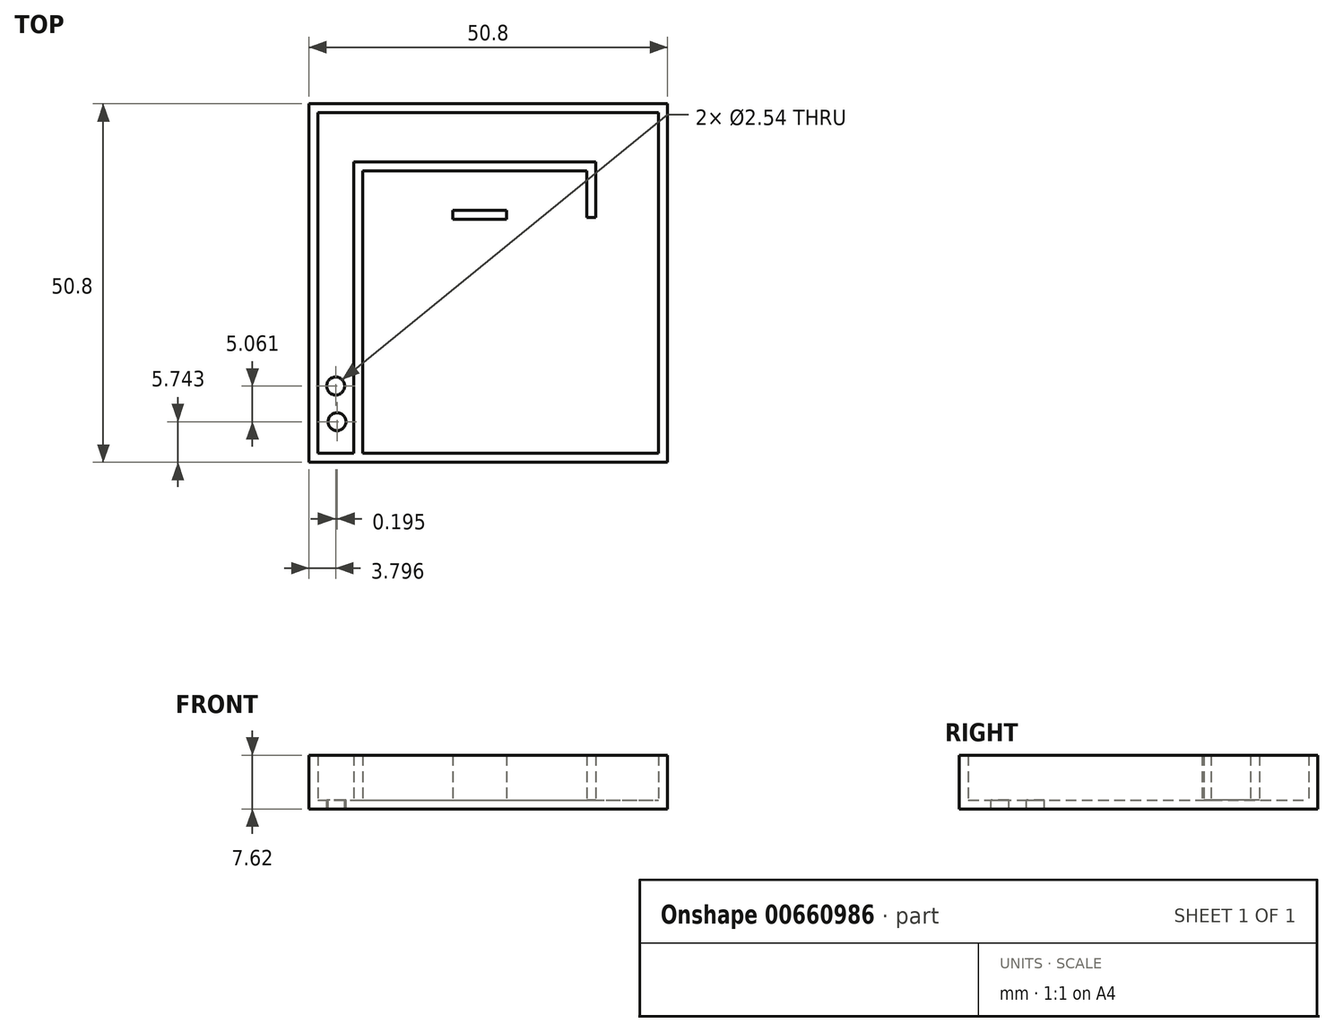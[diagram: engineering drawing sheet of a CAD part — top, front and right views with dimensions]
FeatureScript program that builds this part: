
annotation { "Feature Type Name" : "Feature", "Feature Type Description" : "" }
export const myFeature = defineFeature(function(context is Context, id is Id, definition is map)
    precondition{}
    {
        {
            var Q0;
            Q0=qCreatedBy(makeId("Top.planeOp"),FACE);
            var sketch = newSketch(context, id + "F0", { "sketchPlane" : qUnion([Q0])});
            skLineSegment(sketch, "E0.bottom", {"start": v(0, 0) * mm, "end": v(50.8, 0) * mm});
            skLineSegment(sketch, "E0.top", {"start": v(0, 50.8) * mm, "end": v(50.8, 50.8) * mm});
            skLineSegment(sketch, "E0.left", {"start": v(0, 0) * mm, "end": v(0, 50.8) * mm});
            skLineSegment(sketch, "E0.right", {"start": v(50.8, 0) * mm, "end": v(50.8, 50.8) * mm});
            skSolve(sketch);
        }
        {
            var Q0;
            Q0 = qSketchRegion(id + "F0", true);
            extrude(context, id + "F1", {"entities" : qUnion([Q0]), "depth" : 7.62 * mm, "offsetDistance" : 25.4 * mm});
        }
        {
            var Q0;
            Q0=makeQuery(id+"F1.opExtrude","CAP_FACE",FACE,{"disambiguationData":[OSD([sQuery(id+"F0.wireOp",EDGE,"E0.bottom"),sQuery(id+"F0.wireOp",EDGE,"E0.top"),sQuery(id+"F0.wireOp",EDGE,"E0.left"),sQuery(id+"F0.wireOp",EDGE,"E0.right")])],"isStart":false});
            shell(context, id + "F2", {"entities" : qUnion([Q0]), "thickness" : 1.27 * mm});
        }
        {
            var Q0;
            Q0=makeQuery(id+"F2.opShell","OFFSET_FACE",FACE,{"disambiguationData":[OSD([sQuery(id+"F0.wireOp",EDGE,"E0.bottom"),sQuery(id+"F0.wireOp",EDGE,"E0.top"),sQuery(id+"F0.wireOp",EDGE,"E0.left"),sQuery(id+"F0.wireOp",EDGE,"E0.right")])]});
            var sketch = newSketch(context, id + "F3", { "sketchPlane" : qUnion([Q0])});
            skLineSegment(sketch, "E1", {"start": v(1.27, 1.27) * mm, "end": v(6.35, 1.27) * mm});
            skLineSegment(sketch, "E2.bottom", {"start": v(6.35, 1.27) * mm, "end": v(7.62, 1.27) * mm});
            skLineSegment(sketch, "E2.top", {"start": v(6.35, 42.55) * mm, "end": v(7.62, 42.55) * mm});
            skLineSegment(sketch, "E2.left", {"start": v(6.35, 1.27) * mm, "end": v(6.35, 42.55) * mm});
            skLineSegment(sketch, "E2.right", {"start": v(7.62, 1.27) * mm, "end": v(7.62, 42.55) * mm});
            skLineSegment(sketch, "E3.bottom", {"start": v(7.62, 42.55) * mm, "end": v(40.64, 42.55) * mm});
            skLineSegment(sketch, "E3.top", {"start": v(7.62, 41.28) * mm, "end": v(40.64, 41.28) * mm});
            skLineSegment(sketch, "E3.left", {"start": v(7.62, 42.55) * mm, "end": v(7.62, 41.28) * mm});
            skLineSegment(sketch, "E3.right", {"start": v(40.64, 42.55) * mm, "end": v(40.64, 41.28) * mm});
            skLineSegment(sketch, "E4.bottom", {"start": v(40.64, 41.28) * mm, "end": v(39.37, 41.28) * mm});
            skLineSegment(sketch, "E4.top", {"start": v(40.64, 34.67) * mm, "end": v(39.37, 34.67) * mm});
            skLineSegment(sketch, "E4.left", {"start": v(40.64, 41.28) * mm, "end": v(40.64, 34.67) * mm});
            skLineSegment(sketch, "E4.right", {"start": v(39.37, 41.28) * mm, "end": v(39.37, 34.67) * mm});
            skLineSegment(sketch, "E5.bottom", {"start": v(20.37, 34.42) * mm, "end": v(28, 34.42) * mm});
            skLineSegment(sketch, "E5.top", {"start": v(20.37, 35.69) * mm, "end": v(28, 35.69) * mm});
            skLineSegment(sketch, "E5.left", {"start": v(20.37, 34.42) * mm, "end": v(20.37, 35.69) * mm});
            skLineSegment(sketch, "E5.right", {"start": v(28, 34.42) * mm, "end": v(28, 35.69) * mm});
            skPoint(sketch, "E6.oppositeSnap0", {"position": v(49.53, 25.4) * mm});
            skSolve(sketch);
        }
        {
            var Q0;
            Q0 = qSketchRegion(id + "F3", true);
            extrude(context, id + "F4", {"entities" : qUnion([Q0]), "operationType" : NewBodyOperationType.ADD, "depth" : 6.35 * mm, "offsetDistance" : 25.4 * mm});
        }
        {
            var Q0;
            Q0=makeQuery(id+"F2.opShell","OFFSET_FACE",FACE,{"disambiguationData":[OSD([sQuery(id+"F0.wireOp",EDGE,"E0.bottom"),sQuery(id+"F0.wireOp",EDGE,"E0.top"),sQuery(id+"F0.wireOp",EDGE,"E0.left"),sQuery(id+"F0.wireOp",EDGE,"E0.right")])]});
            var sketch = newSketch(context, id + "F5", { "sketchPlane" : qUnion([Q0])});
            skCircle(sketch, "E7", {"center": v(4, 5.74) * mm, "radius": 1.27 * mm});
            skCircle(sketch, "E8", {"center": v(3.8, 10.8) * mm, "radius": 1.27 * mm});
            skSolve(sketch);
        }
        {
            var Q0;
            Q0 = qSketchRegion(id + "F5", true);
            extrude(context, id + "F6", {"entities" : qUnion([Q0]), "operationType" : NewBodyOperationType.REMOVE, "oppositeDirection" : true, "depth" : 25.4 * mm, "offsetDistance" : 25.4 * mm});
        }
    });
